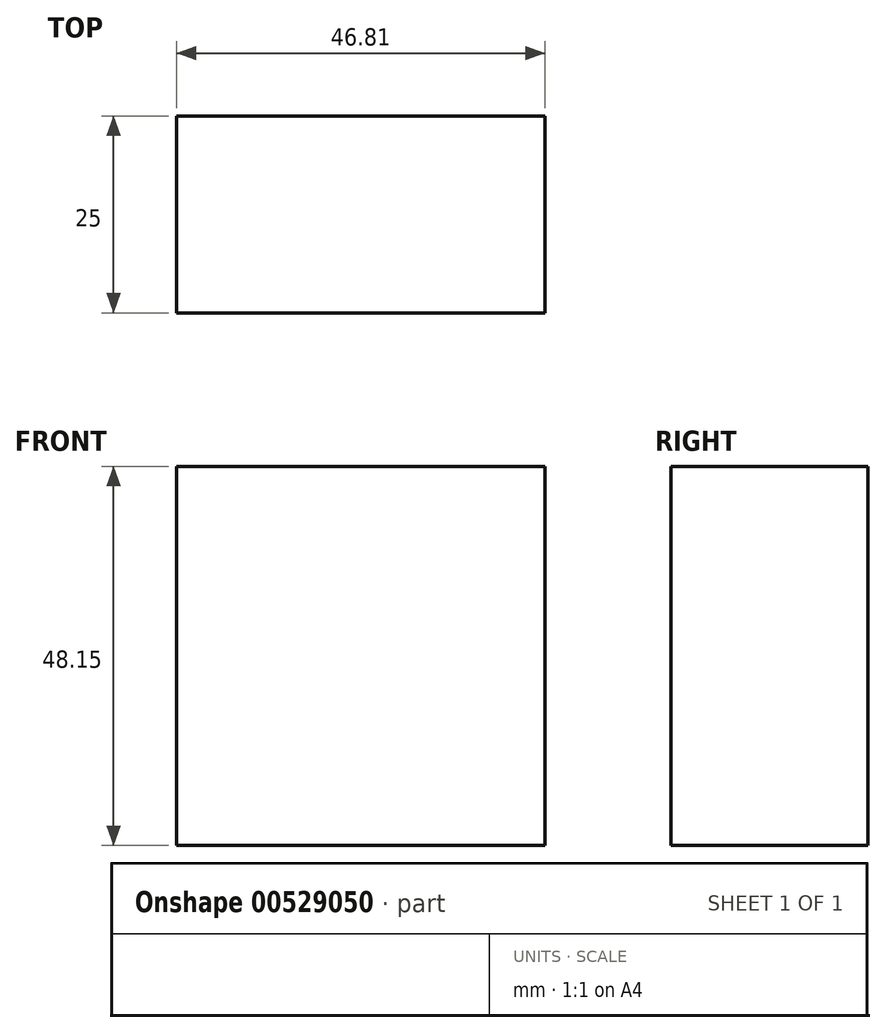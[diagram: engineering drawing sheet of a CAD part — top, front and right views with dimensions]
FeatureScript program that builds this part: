
annotation { "Feature Type Name" : "Feature", "Feature Type Description" : "" }
export const myFeature = defineFeature(function(context is Context, id is Id, definition is map)
    precondition{}
    {
        {
            var Q0;
            Q0=qCreatedBy(makeId("Front.planeOp"),FACE);
            var sketch = newSketch(context, id + "F0", { "sketchPlane" : qUnion([Q0])});
            skLineSegment(sketch, "E0.bottom", {"start": v(0, 0) * mm, "end": v(46.81, 0) * mm});
            skLineSegment(sketch, "E0.top", {"start": v(0, -48.15) * mm, "end": v(46.81, -48.15) * mm});
            skLineSegment(sketch, "E0.left", {"start": v(0, 0) * mm, "end": v(0, -48.15) * mm});
            skLineSegment(sketch, "E0.right", {"start": v(46.81, 0) * mm, "end": v(46.81, -48.15) * mm});
            skSolve(sketch);
        }
        {
            var Q0;
            Q0=makeQuery(id+"F0.imprint","IMPRINT",FACE,{"disambiguationData":[TD([[makeQuery(id+"F0.imprint","IMPRINT",EDGE,{"derivedFrom":sQuery(id+"F0.wireOp",EDGE,"E0.bottom")}),-1.0]])]});
            extrude(context, id + "F1", {"entities" : qUnion([Q0]), "depth" : 25 * mm, "offsetDistance" : 25 * mm});
        }
    });
